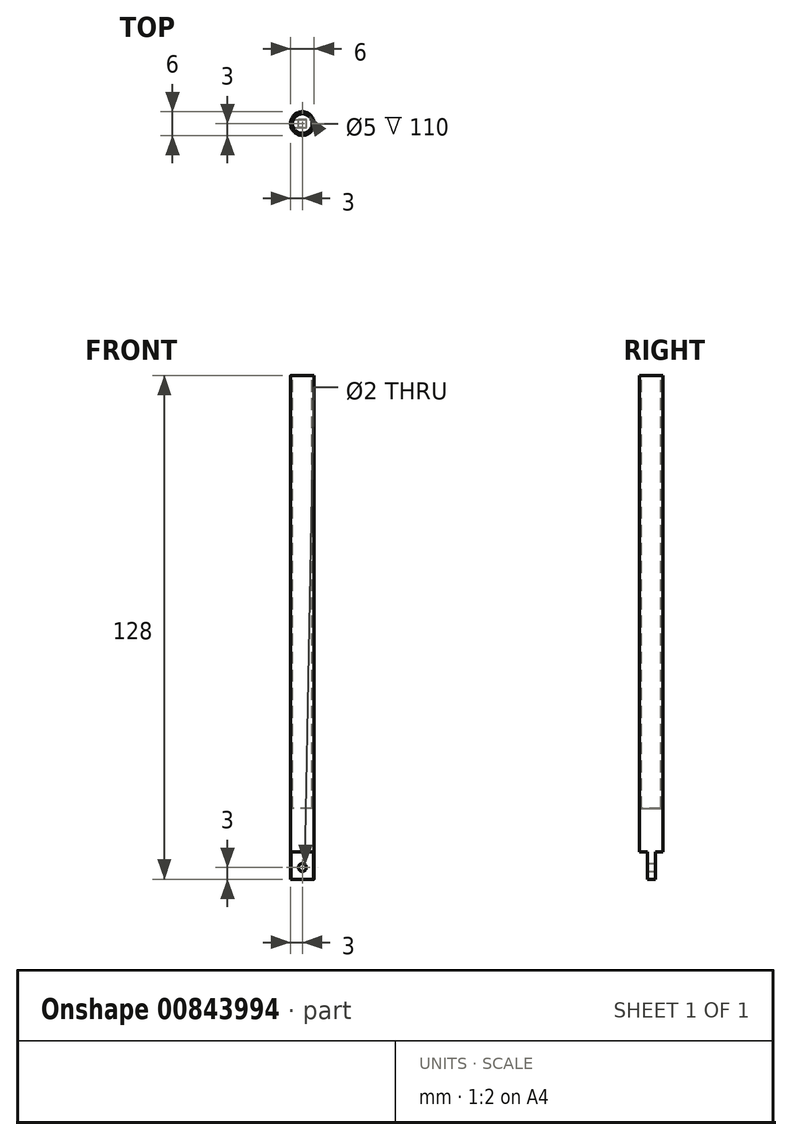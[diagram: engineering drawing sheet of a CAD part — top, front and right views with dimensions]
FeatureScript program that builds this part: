
annotation { "Feature Type Name" : "Feature", "Feature Type Description" : "" }
export const myFeature = defineFeature(function(context is Context, id is Id, definition is map)
    precondition{}
    {
        {
            var Q0;
            Q0=qCreatedBy(makeId("Top.planeOp"),FACE);
            var sketch = newSketch(context, id + "F0", { "sketchPlane" : qUnion([Q0])});
            skCircle(sketch, "E0", {"center": v(0, 0) * mm, "radius": 3 * mm});
            skSolve(sketch);
        }
        {
            var Q0;
            Q0=makeQuery(id+"F0.imprint","IMPRINT",FACE,{"disambiguationData":[TD([[makeQuery(id+"F0.imprint","IMPRINT",EDGE,{"derivedFrom":sQuery(id+"F0.wireOp",EDGE,"E0")}),1.0]])]});
            extrude(context, id + "F1", {"entities" : qUnion([Q0]), "depth" : 128 * mm, "offsetDistance" : 25 * mm});
        }
        {
            var Q0;
            Q0=qCreatedBy(makeId("Right.planeOp"),FACE);
            var sketch = newSketch(context, id + "F2", { "sketchPlane" : qUnion([Q0])});
            skPoint(sketch, "E1.middle", {"position": v(-1.97, 8.05) * mm});
            skLineSegment(sketch, "E2", {"start": v(-1, 7) * mm, "end": v(-1, 0) * mm});
            skLineSegment(sketch, "E3", {"start": v(-1, 7) * mm, "end": v(-3, 7) * mm});
            skLineSegment(sketch, "E4", {"start": v(-3, 7) * mm, "end": v(-3, 0) * mm});
            skLineSegment(sketch, "E5", {"start": v(-3, 0) * mm, "end": v(-1, 0) * mm});
            skLineSegment(sketch, "E6", {"start": v(1, 7) * mm, "end": v(1, 0) * mm});
            skLineSegment(sketch, "E7", {"start": v(3, 0) * mm, "end": v(3, 7) * mm});
            skLineSegment(sketch, "E8", {"start": v(3, 7) * mm, "end": v(1, 7) * mm});
            skLineSegment(sketch, "E9", {"start": v(1, 0) * mm, "end": v(3, 0) * mm});
            skSolve(sketch);
        }
        {
            var Q0;
            Q0 = qSketchRegion(id + "F2", true);
            extrude(context, id + "F3", {"entities" : qUnion([Q0]), "operationType" : NewBodyOperationType.REMOVE, "endBound" : BoundingType.SYMMETRIC, "oppositeDirection" : true, "depth" : 25 * mm, "offsetDistance" : 25 * mm});
        }
        {
            var Q0;
            Q0=makeQuery(id+"F3.boolean.opBoolean","COPY",FACE,{"derivedFrom":makeQuery(id+"F3.opExtrude","SWEPT_FACE",FACE,{"disambiguationData":[OSD([sQuery(id+"F2.wireOp",EDGE,"E6")])]})});
            var sketch = newSketch(context, id + "F4", { "sketchPlane" : qUnion([Q0])});
            skCircle(sketch, "E10", {"center": v(0, 3) * mm, "radius": 1 * mm});
            skSolve(sketch);
        }
        {
            var Q0;
            Q0 = qSketchRegion(id + "F4", true);
            extrude(context, id + "F5", {"entities" : qUnion([Q0]), "operationType" : NewBodyOperationType.REMOVE, "oppositeDirection" : true, "depth" : 25 * mm, "offsetDistance" : 25 * mm});
        }
        {
            var Q0;
            Q0=makeQuery(id+"F1.opExtrude","CAP_FACE",FACE,{"disambiguationData":[OSD([sQuery(id+"F0.wireOp",EDGE,"E0")])],"isStart":false});
            var sketch = newSketch(context, id + "F6", { "sketchPlane" : qUnion([Q0])});
            skCircle(sketch, "E11", {"center": v(0, 0) * mm, "radius": 2.5 * mm});
            skSolve(sketch);
        }
        {
            var Q0;
            Q0=makeQuery(id+"F6.imprint","IMPRINT",FACE,{"disambiguationData":[TD([[makeQuery(id+"F6.imprint","IMPRINT",EDGE,{"derivedFrom":sQuery(id+"F6.wireOp",EDGE,"E11")}),1.0]])]});
            extrude(context, id + "F7", {"entities" : qUnion([Q0]), "operationType" : NewBodyOperationType.REMOVE, "oppositeDirection" : true, "depth" : 110 * mm, "offsetDistance" : 25 * mm});
        }
    });
